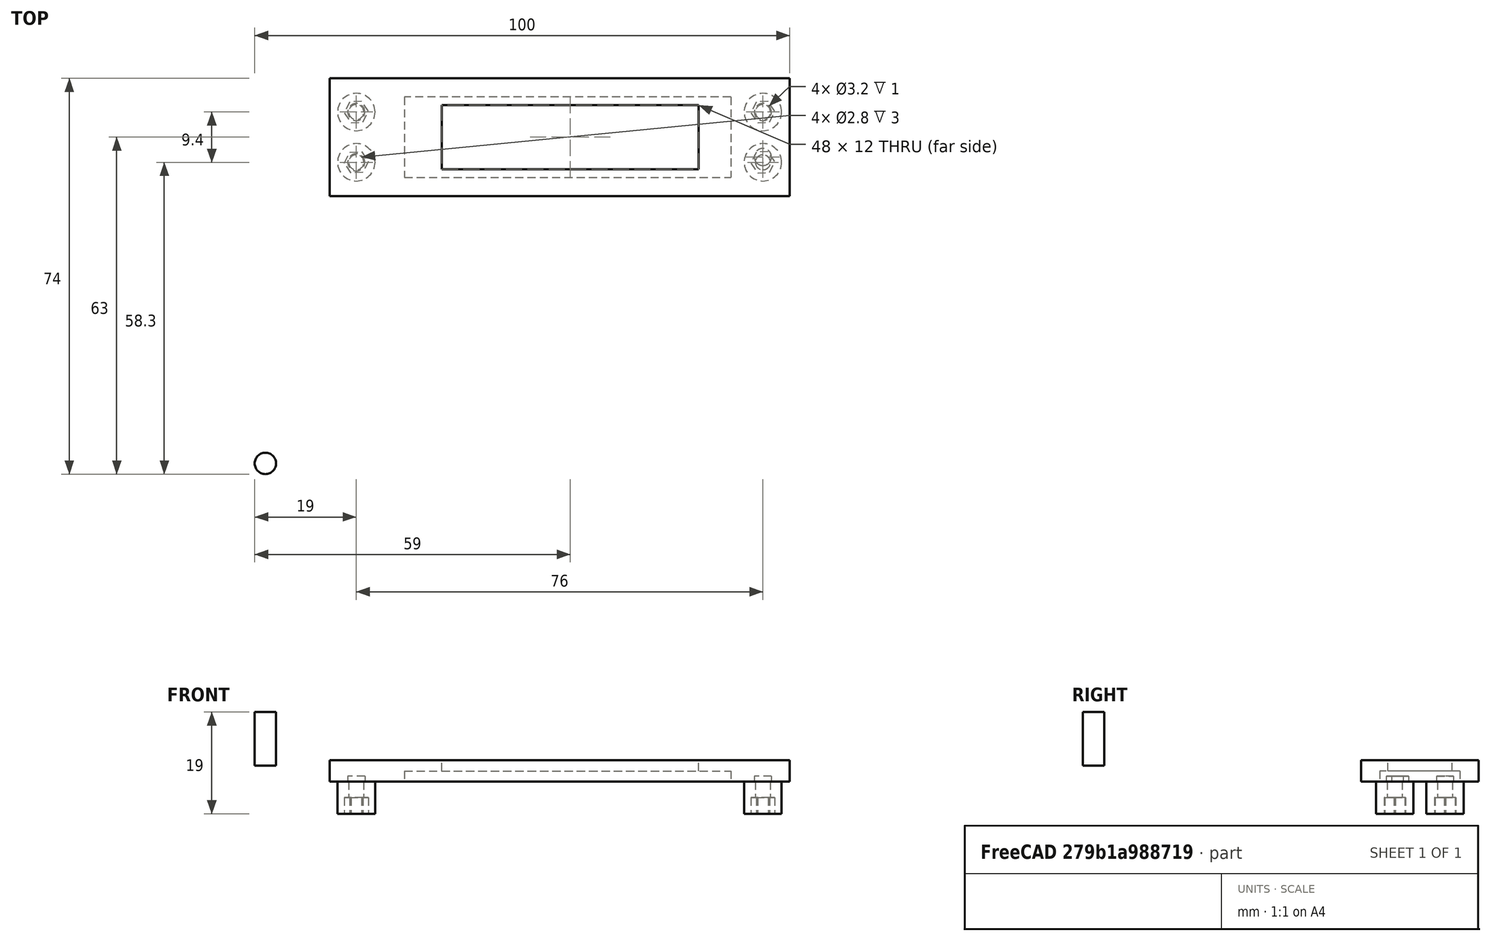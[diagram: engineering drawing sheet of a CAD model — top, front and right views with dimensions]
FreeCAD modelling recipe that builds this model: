
FCSTD DOCUMENT  (FreeCAD 0.17R13522 (Git))
Label: test_panel_display
License: CreativeCommons Attribution-ShareAlike
LicenseURL: http://creativecommons.org/licenses/by-sa/4.0/
objects: Part::Feature×34, Part::Fuse×28, Part::Cut×16, Part::Part2DObjectPython×10, Part::Box×6, Part::FeaturePython×4, Part::Cylinder×1, Part::Extrusion×1, App::DocumentObjectGroup×1
note: 100 computed .brp shape members not serialized (recipe doc carries the construction recipe); baked Part::Feature solids carry a one-line shape summary decoded from their .brp

FEATURE [Part::Box] Box  label="base principal"
  AttacherType = Attacher::AttachEngine3D
  Height = 4
  Length = 280
  Placement = pos=(0,0,-4) rot=(0,0,1;0rad)
  Width = 210
FEATURE [Part::Feature] Fusion008001001  label="perforador encoder"
  Placement = pos=(17,17,-6) rot=(1,0,0;3.14159rad)
  shape: bbox 82.5 x 15 x 10 mm, 18 faces (baked)
FEATURE [Part::Feature] Fusion008001001001  label="perforador active 1"
  Placement = pos=(17,98,-6) rot=(1,0,0;3.14159rad)
  shape: bbox 82.5 x 15 x 10 mm, 18 faces (baked)
FEATURE [Part::Feature] Fusion008001001002  label="perforador active 2"
  Placement = pos=(17,57.5,-6) rot=(1,0,0;3.14159rad)
  shape: bbox 82.5 x 15 x 10 mm, 18 faces (baked)
FEATURE [Part::Feature] Fusion008001001003  label="perforador standby 1"
  Placement = pos=(136,98,-6) rot=(1,0,0;3.14159rad)
  shape: bbox 82.5 x 15 x 10 mm, 18 faces (baked)
FEATURE [Part::Feature] Fusion008001001004  label="perforador standby 2"
  Placement = pos=(136,57.5,-6) rot=(1,0,0;3.14159rad)
  shape: bbox 82.5 x 15 x 10 mm, 18 faces (baked)
FEATURE [Part::Cut] Cut
  Base = -> Box
  Refine = true
  Tool = -> Fusion008001001
FEATURE [Part::Cut] Cut001
  Base = -> Cut
  Refine = true
  Tool = -> Fusion008001001001
FEATURE [Part::Cut] Cut002
  Base = -> Cut001
  Refine = true
  Tool = -> Fusion008001001002
FEATURE [Part::Cut] Cut003
  Base = -> Cut002
  Refine = true
  Tool = -> Fusion008001001003
FEATURE [Part::Cut] Cut004  label="base con 7 segmentos sin frente perforado"
  Base = -> Cut003
  Refine = true
  Tool = -> Fusion008001001004
FEATURE [Part::Feature] BooleanFragments001  label="perforador encoder izquierda"
  Placement = pos=(130,20.2,4) rot=(0,0,1;0rad)
  shape: bbox 45.2 x 30 x 10 mm, 34 faces, 4 solids (baked)
FEATURE [Part::Feature] BooleanFragments002  label="perforador encoder derecha"
  Placement = pos=(178,20.2,4) rot=(0,0,1;0rad)
  shape: bbox 45.2 x 30 x 10 mm, 34 faces, 4 solids (baked)
FEATURE [Part::Cut] Cut005
  Base = -> Cut004
  Refine = true
  Tool = -> BooleanFragments001
FEATURE [Part::Cut] Cut006  label="frente con agujeros displays y encoders transponder"
  Base = -> Cut005
  Refine = true
  Tool = -> BooleanFragments002
FEATURE [Part::Feature] Fusion005001  label="boton ident"
  Placement = pos=(203,14.2,1) rot=(0,0,1;0rad)
  shape: bbox 30 x 12 x 10 mm, 14 faces (baked)
FEATURE [Part::Cut] Cut007
  Base = -> Cut006
  Refine = true
  Tool = -> Fusion005001
FEATURE [Part::Part2DObjectPython] Line009  # Draft 2D object (typed FeaturePython)
  ChamferSize = 0
  Closed = false
  End = (270.847,20.2,0)
  FilletRadius = 0
  Length = 35.3471
  MakeFace = false
  Points = (2) [(235.5,20.2,0),(270.847,20.2,0)]
  Start = (235.5,20.2,0)
  Subdivisions = 0
FEATURE [Part::Cylinder] Cylinder
  Angle = 360
  AttacherType = Attacher::AttachEngine3D
  Height = 10
  Radius = 2
FEATURE [Part::Part2DObjectPython] Circle  # Draft 2D object (typed FeaturePython)
  FirstAngle = 0
  LastAngle = 0
  MakeFace = false
  Placement = pos=(269.619,20.2,4) rot=(0,0,1;0rad)
  Radius = 4.75
FEATURE [Part::Part2DObjectPython] Circle001  # Draft 2D object (typed FeaturePython)
  FirstAngle = 0
  LastAngle = 0
  MakeFace = false
  Placement = pos=(259.67,20.2,0) rot=(0,0,1;0rad)
  Radius = 14
FEATURE [Part::Extrusion] Extrude
  Base = -> Circle
  Dir = (0,0,1)
  DirMode = 2
  FaceMakerClass = Part::FaceMakerBullseye
  LengthFwd = 10
  LengthRev = 0
  Placement = pos=(-10,0,-10) rot=(0,0,1;0rad)
  Solid = true
  Symmetric = false
FEATURE [Part::Part2DObjectPython] Line014  # Draft 2D object (typed FeaturePython)
  ChamferSize = 0
  Closed = false
  End = (248.272,28.2144,0)
  FilletRadius = 0
  Length = 13.696
  MakeFace = false
  Placement = pos=(-10,0,-4) rot=(0,0,1;0rad)
  Points = (2) [(269.378,20.2,4),(258.272,28.2144,4)]
  Start = (259.378,20.2,0)
  Subdivisions = 0
FEATURE [Part::Part2DObjectPython] Line015  # Draft 2D object (typed FeaturePython)
  ChamferSize = 0
  Closed = false
  End = (254.876,33.263,0)
  FilletRadius = 0
  Length = 13.7518
  MakeFace = false
  Placement = pos=(-10,0,-4) rot=(0,0,1;0rad)
  Points = (2) [(269.174,20.2,4),(264.876,33.263,4)]
  Start = (259.174,20.2,0)
  Subdivisions = 0
FEATURE [Part::Part2DObjectPython] Line016  # Draft 2D object (typed FeaturePython)
  ChamferSize = 0
  Closed = false
  End = (263.227,33.6931,0)
  FilletRadius = 0
  Length = 14.1488
  MakeFace = false
  Placement = pos=(-10,0,-4) rot=(0,0,1;0rad)
  Points = (2) [(268.97,20.2,4),(273.227,33.6931,4)]
  Start = (258.97,20.2,0)
  Subdivisions = 0
FEATURE [Part::Part2DObjectPython] Line017  # Draft 2D object (typed FeaturePython)
  ChamferSize = 0
  Closed = false
  End = (270.612,28.9289,0)
  FilletRadius = 0
  Length = 14.5511
  MakeFace = false
  Placement = pos=(-10,0,-4) rot=(0,0,1;0rad)
  Points = (2) [(268.97,20.2,4),(280.612,28.9289,4)]
  Start = (258.97,20.2,0)
  Subdivisions = 0
FEATURE [Part::Part2DObjectPython] Line  # Draft 2D object (typed FeaturePython)
  ChamferSize = 0
  Closed = true
  End = (269.619,20.2,0)
  FilletRadius = 0
  Length = 0
  MakeFace = false
  Points = (2) [(269.619,20.2,0),(269.619,20.2,0)]
  Start = (269.619,20.2,0)
  Subdivisions = 0
FEATURE [Part::Cut] Cut008  label="base con line inferior completa"
  Base = -> Cut007
  Refine = true
  Tool = -> Extrude
FEATURE [Part::Part2DObjectPython] Line019  # Draft 2D object (typed FeaturePython)
  ChamferSize = 0
  Closed = false
  End = (259.619,169.66,0)
  FilletRadius = 0
  Length = 149.46
  MakeFace = true
  Placement = pos=(-20,0,-10) rot=(0,0,1;0rad)
  Points = (2) [(279.619,20.2,10),(279.619,169.66,10)]
  Start = (259.619,20.2,0)
  Subdivisions = 0
FEATURE [Part::Part2DObjectPython] Line023  # Draft 2D object (typed FeaturePython)
  ChamferSize = 0
  Closed = false
  End = (270.85,61,0)
  FilletRadius = 0
  Length = 96.85
  MakeFace = false
  Points = (2) [(174,61,0),(270.85,61,0)]
  Start = (174,61,0)
  Subdivisions = 0
FEATURE [App::DocumentObjectGroup] Construction
  Group = -> [Line009,Circle001,Line014,Line015,Line016,Line017,Line,Line019,Line023]
FEATURE [Part::Feature] BooleanFragments003  label="perforador para comunication 1"
  Placement = pos=(251.8,102,3) rot=(0,0,1;3.14159rad)
  shape: bbox 45.2 x 30 x 10 mm, 34 faces, 4 solids (baked)
FEATURE [Part::Feature] BooleanFragments003001  label="perforador para comunication 2"
  Placement = pos=(251.8,61,4) rot=(0,0,1;3.14159rad)
  shape: bbox 45.2 x 30 x 10 mm, 34 faces, 4 solids (baked)
FEATURE [Part::Cut] Cut009
  Base = -> Cut008
  Refine = true
  Tool = -> BooleanFragments003001
FEATURE [Part::Cut] Cut010  label="panel sin botones y sin leds"
  Base = -> Cut009
  Refine = true
  Tool = -> BooleanFragments003
FEATURE [Part::Feature] Cut001001  label="the_spacer_1mm_inside"
  Placement = pos=(17,106.2,0) rot=(0.99953,0.030644,0;3.14159rad)
  shape: bbox 7 x 7 x 6 mm, 11 faces (baked)
FEATURE [Part::Fuse] Fusion
  Base = -> Cut010
  Refine = true
  Tool = -> Cut001001
FEATURE [Part::Fuse] Fusion008001001005
  Base = -> Fusion
  Refine = true
FEATURE [Part::Feature] Cut001001001  label="the_spacer_1mm_inside001"
  Placement = pos=(17,96.8,0) rot=(0.99953,0.030644,0;3.14159rad)
  shape: bbox 7 x 7 x 6 mm, 11 faces (baked)
FEATURE [Part::Fuse] Fusion008001001006
  Base = -> Fusion008001001005
  Refine = true
  Tool = -> Cut001001001
FEATURE [Part::Fuse] Fusion008001001007
  Placement = pos=(0,0,1) rot=(0,0,1;0rad)
  Refine = true
  Tool = -> Fusion008001001006
FEATURE [Part::Feature] Cut001001001001  label="the_spacer_1mm_inside002"
  Placement = pos=(17,56.3,0) rot=(0.99953,0.030644,0;3.14159rad)
  shape: bbox 7 x 7 x 6 mm, 11 faces (baked)
FEATURE [Part::Feature] Cut001001001002  label="the_spacer_1mm_inside003"
  Placement = pos=(17,65.7,0) rot=(0.99953,0.030644,0;3.14159rad)
  shape: bbox 7 x 7 x 6 mm, 11 faces (baked)
FEATURE [Part::Feature] Cut001001001002001  label="the_spacer_1mm_inside004"
  Placement = pos=(17,25.2,0) rot=(0.99953,0.030644,0;3.14159rad)
  shape: bbox 7 x 7 x 6 mm, 11 faces (baked)
FEATURE [Part::Feature] Cut001001001001001  label="the_spacer_1mm_inside005"
  Placement = pos=(17,15.8,0) rot=(0.99953,0.030644,0;3.14159rad)
  shape: bbox 7 x 7 x 6 mm, 11 faces (baked)
FEATURE [Part::Feature] Cut001001001002002  label="the_spacer_1mm_inside006"
  Placement = pos=(136,106.2,0) rot=(0.99953,0.030644,0;3.14159rad)
  shape: bbox 7 x 7 x 6 mm, 11 faces (baked)
FEATURE [Part::Feature] Cut001001001002003  label="the_spacer_1mm_inside007"
  Placement = pos=(136,96.8,0) rot=(0.99953,0.030644,0;3.14159rad)
  shape: bbox 7 x 7 x 6 mm, 11 faces (baked)
FEATURE [Part::Feature] Cut001001001002004  label="the_spacer_1mm_inside008"
  Placement = pos=(136,65.7,0) rot=(0.99953,0.030644,0;3.14159rad)
  shape: bbox 7 x 7 x 6 mm, 11 faces (baked)
FEATURE [Part::Feature] Cut001001001001002  label="the_spacer_1mm_inside009"
  Placement = pos=(136,56.3,0) rot=(0.99953,0.030644,0;3.14159rad)
  shape: bbox 7 x 7 x 6 mm, 11 faces (baked)
FEATURE [Part::Feature] Cut001001001001002001  label="the_spacer_1mm_inside010"
  Placement = pos=(93,65.7,0) rot=(0.99953,0.030644,0;3.14159rad)
  shape: bbox 7 x 7 x 6 mm, 11 faces (baked)
FEATURE [Part::Feature] Cut001001001002002001  label="the_spacer_1mm_inside011"
  Placement = pos=(93,106.2,0) rot=(0.99953,0.030644,0;3.14159rad)
  shape: bbox 7 x 7 x 6 mm, 11 faces (baked)
FEATURE [Part::Feature] Cut001001001002003001  label="the_spacer_1mm_inside012"
  Placement = pos=(93,96.8,0) rot=(0.99953,0.030644,0;3.14159rad)
  shape: bbox 7 x 7 x 6 mm, 11 faces (baked)
FEATURE [Part::Feature] Cut001001001001002002  label="the_spacer_1mm_inside013"
  Placement = pos=(93,56.3,0) rot=(0.99953,0.030644,0;3.14159rad)
  shape: bbox 7 x 7 x 6 mm, 11 faces (baked)
FEATURE [Part::Feature] Cut001001001002001001  label="the_spacer_1mm_inside014"
  Placement = pos=(93,25.2,0) rot=(0.99953,0.030644,0;3.14159rad)
  shape: bbox 7 x 7 x 6 mm, 11 faces (baked)
FEATURE [Part::Feature] Cut001001001001001001  label="the_spacer_1mm_inside015"
  Placement = pos=(93,15.8,0) rot=(0.99953,0.030644,0;3.14159rad)
  shape: bbox 7 x 7 x 6 mm, 11 faces (baked)
FEATURE [Part::Feature] Cut001001001002002001001  label="the_spacer_1mm_inside016"
  Placement = pos=(212,106.2,0) rot=(0.99953,0.030644,0;3.14159rad)
  shape: bbox 7 x 7 x 6 mm, 11 faces (baked)
FEATURE [Part::Feature] Cut001001001002003001001  label="the_spacer_1mm_inside017"
  Placement = pos=(212,96.8,0) rot=(0.99953,0.030644,0;3.14159rad)
  shape: bbox 7 x 7 x 6 mm, 11 faces (baked)
FEATURE [Part::Feature] Cut001001001001002001001  label="the_spacer_1mm_inside018"
  Placement = pos=(212,65.7,0) rot=(0.99953,0.030644,0;3.14159rad)
  shape: bbox 7 x 7 x 6 mm, 11 faces (baked)
FEATURE [Part::Feature] Cut001001001001002002001  label="the_spacer_1mm_inside019"
  Placement = pos=(212,56.3,0) rot=(0.99953,0.030644,0;3.14159rad)
  shape: bbox 7 x 7 x 6 mm, 11 faces (baked)
FEATURE [Part::Fuse] Fusion008001001008
  Base = -> Cut001001001001
  Refine = true
  Tool = -> Cut001001001002
FEATURE [Part::Fuse] Fusion008001001009
  Base = -> Cut001001001002001
  Refine = true
  Tool = -> Cut001001001001001
FEATURE [Part::Fuse] Fusion008001001010
  Base = -> Cut001001001002002001
  Refine = true
  Tool = -> Cut001001001002003001
FEATURE [Part::Fuse] Fusion008001001011
  Base = -> Cut001001001002002001
  Refine = true
  Tool = -> Cut001001001002003001
FEATURE [Part::Fuse] Fusion008001001012
  Base = -> Cut001001001001002001
  Refine = true
  Tool = -> Cut001001001001002002
FEATURE [Part::Fuse] Fusion008001001013
  Base = -> Cut001001001002001001
  Refine = true
  Tool = -> Cut001001001001001001
FEATURE [Part::Fuse] Fusion008001001014
  Base = -> Cut001001001002002
  Refine = true
  Tool = -> Cut001001001002003
FEATURE [Part::Fuse] Fusion008001001015
  Base = -> Cut001001001002002
  Refine = true
  Tool = -> Cut001001001002003
FEATURE [Part::Fuse] Fusion008001001016
  Base = -> Cut001001001002004
  Refine = true
  Tool = -> Cut001001001001002
FEATURE [Part::Fuse] Fusion008001001017
  Base = -> Cut001001001002002001001
  Refine = true
  Tool = -> Cut001001001002003001001
FEATURE [Part::Fuse] Fusion008001001018
  Base = -> Cut001001001001002001001
  Refine = true
  Tool = -> Cut001001001001002002001
FEATURE [Part::FeaturePython] BooleanFragments  # WARN: FeaturePython — macro-defined, semantics opaque (R4)
  Mode = 0
  Objects = -> [Fusion008001001007,Fusion008001001008]
  Tolerance = 0
FEATURE [Part::FeaturePython] BooleanFragments003002  # WARN: FeaturePython — macro-defined, semantics opaque (R4)
  Mode = 0
  Objects = -> [BooleanFragments,Fusion008001001009]
  Tolerance = 0
FEATURE [Part::FeaturePython] BooleanFragments003003  # WARN: FeaturePython — macro-defined, semantics opaque (R4)
  Mode = 0
  Objects = -> [BooleanFragments003002,Fusion008001001010]
  Tolerance = 0
FEATURE [Part::FeaturePython] BooleanFragments003004  # WARN: FeaturePython — macro-defined, semantics opaque (R4)
  Mode = 0
  Objects = -> [BooleanFragments003003,Fusion008001001012]
  Tolerance = 0
FEATURE [Part::Fuse] Fusion008001001019
  Base = -> Fusion008001001013
  Refine = true
  Tool = -> BooleanFragments003004
FEATURE [Part::Fuse] Fusion008001001020
  Base = -> Fusion008001001014
  Refine = true
  Tool = -> Fusion008001001019
FEATURE [Part::Fuse] Fusion008001001021
  Base = -> Fusion008001001014
  Refine = true
  Tool = -> Fusion008001001019
FEATURE [Part::Fuse] Fusion008001001022
  Base = -> Fusion008001001011
  Refine = true
  Tool = -> Fusion008001001020
FEATURE [Part::Fuse] Fusion008001001023
  Base = -> Fusion008001001021
  Refine = true
  Tool = -> Fusion008001001022
FEATURE [Part::Fuse] Fusion008001001024
  Base = -> Fusion008001001016
  Refine = true
  Tool = -> Fusion008001001023
FEATURE [Part::Fuse] Fusion008001001025
  Base = -> Fusion008001001017
  Refine = true
  Tool = -> Fusion008001001024
FEATURE [Part::Fuse] Fusion008001001026
  Base = -> Fusion008001001018
  Refine = true
  Tool = -> Fusion008001001025
FEATURE [Part::Fuse] Fusion008001001027
  Base = -> Fusion008001001015
  Refine = true
  Tool = -> Fusion008001001026
FEATURE [Part::Feature] Box001001001  label="Cube002"
  Placement = pos=(14,53.5,-2) rot=(0,0,1;0rad)
  shape: bbox 6 x 6 x 3 mm, 6 faces (baked)
FEATURE [Part::Feature] Box001001002  label="Cube003"
  Placement = pos=(14,62.5,-2) rot=(0,0,1;0rad)
  shape: bbox 6 x 6 x 3 mm, 6 faces (baked)
FEATURE [Part::Feature] Box001001001001  label="Cube004"
  Placement = pos=(90,54,-2) rot=(0,0,1;0rad)
  shape: bbox 6 x 6 x 3 mm, 6 faces (baked)
FEATURE [Part::Feature] Box001001002001  label="Cube005"
  Placement = pos=(90,63,-2) rot=(0,0,1;0rad)
  shape: bbox 6 x 6 x 3 mm, 6 faces (baked)
FEATURE [Part::Box] Box001001002002002  label="Cube010"
  AttacherType = Attacher::AttachEngine3D
  Height = 30
  Length = 300
  Placement = pos=(-13,0,-16) rot=(0,0,1;0rad)
  Width = 50
FEATURE [Part::Cut] Cut001001001002003001002
  Base = -> Fusion008001001027
  Refine = true
  Tool = -> Box001001002002002
FEATURE [Part::Fuse] Fusion008001001028
  Base = -> Box001001001001
  Refine = true
  Tool = -> Cut001001001002003001002
FEATURE [Part::Fuse] Fusion008001001029
  Base = -> Box001001002001
  Refine = true
  Tool = -> Fusion008001001028
FEATURE [Part::Box] Box001001002002003  label="Cube011"
  AttacherType = Attacher::AttachEngine3D
  Height = 30
  Length = 300
  Placement = pos=(-10,72,-14) rot=(0,0,1;0rad)
  Width = 150
FEATURE [Part::Cut] Cut001001001002003001003
  Base = -> Fusion008001001029
  Refine = true
  Tool = -> Box001001002002003
FEATURE [Part::Box] Box001001002002004  label="Cube"
  AttacherType = Attacher::AttachEngine3D
  Height = 30
  Length = 200
  Placement = pos=(98,0,-22) rot=(0,0,1;0rad)
  Width = 100
FEATURE [Part::Cut] Cut001001001002003001004
  Base = -> Cut001001001002003001003
  Refine = true
  Tool = -> Box001001002002004
FEATURE [Part::Box] Box001001002002005  label="Cube012"
  AttacherType = Attacher::AttachEngine3D
  Height = 30
  Length = 49
  Placement = pos=(-37,-1,-7) rot=(0,0,1;0rad)
  Width = 100
FEATURE [Part::Cut] Cut001001001002003001005
  Base = -> Cut001001001002003001004
  Refine = true
  Tool = -> Box001001002002005
FEATURE [Part::Box] Box001001002002006  label="Cube013"
  AttacherType = Attacher::AttachEngine3D
  Height = 30
  Length = 48
  Placement = pos=(33,55,-4) rot=(0,0,1;0rad)
  Width = 12
FEATURE [Part::Cut] Cut001001001002003001006
  Base = -> Cut001001001002003001005
  Refine = true
  Tool = -> Box001001002002006
FEATURE [Part::Fuse] Fusion008001001030
  Base = -> Box001001002
  Refine = true
  Tool = -> Cut001001001002003001006
FEATURE [Part::Fuse] Fusion008001001031
  Base = -> Box001001001
  Refine = true
  Tool = -> Fusion008001001030
